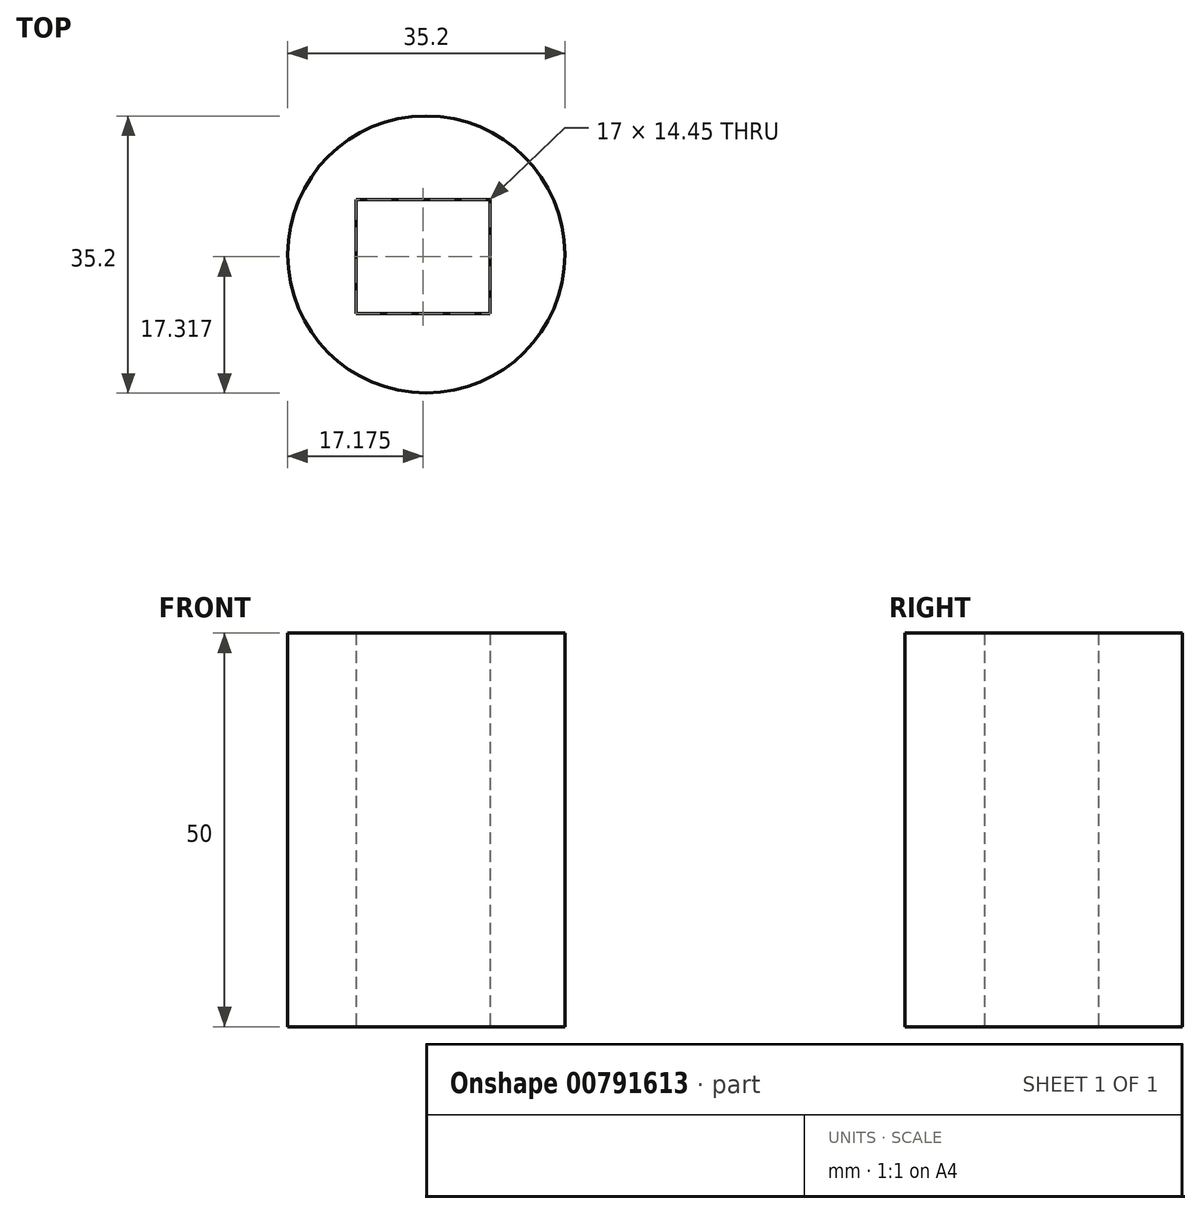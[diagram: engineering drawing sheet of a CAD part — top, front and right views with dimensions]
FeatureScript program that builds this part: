
annotation { "Feature Type Name" : "Feature", "Feature Type Description" : "" }
export const myFeature = defineFeature(function(context is Context, id is Id, definition is map)
    precondition{}
    {
        {
            var Q0;
            Q0=qCreatedBy(makeId("Top.planeOp"),FACE);
            var sketch = newSketch(context, id + "F0", { "sketchPlane" : qUnion([Q0])});
            skCircle(sketch, "E0", {"center": v(0, 0) * mm, "radius": 17.6 * mm});
            skLineSegment(sketch, "E1.bottom", {"start": v(-8.92, 6.94) * mm, "end": v(8.07, 6.94) * mm});
            skLineSegment(sketch, "E1.top", {"start": v(-8.92, -7.5) * mm, "end": v(8.07, -7.5) * mm});
            skLineSegment(sketch, "E1.left", {"start": v(-8.92, 6.94) * mm, "end": v(-8.92, -7.5) * mm});
            skLineSegment(sketch, "E1.right", {"start": v(8.07, 6.94) * mm, "end": v(8.07, -7.5) * mm});
            skSolve(sketch);
        }
        {
            var Q0;
            Q0=makeQuery(id+"F0.imprint","IMPRINT",FACE,{"disambiguationData":[TD([[makeQuery(id+"F0.imprint","IMPRINT",EDGE,{"derivedFrom":sQuery(id+"F0.wireOp",EDGE,"E0")}),1.0]])]});
            extrude(context, id + "F1", {"entities" : qUnion([Q0]), "depth" : 50 * mm, "offsetDistance" : 25 * mm});
        }
    });
